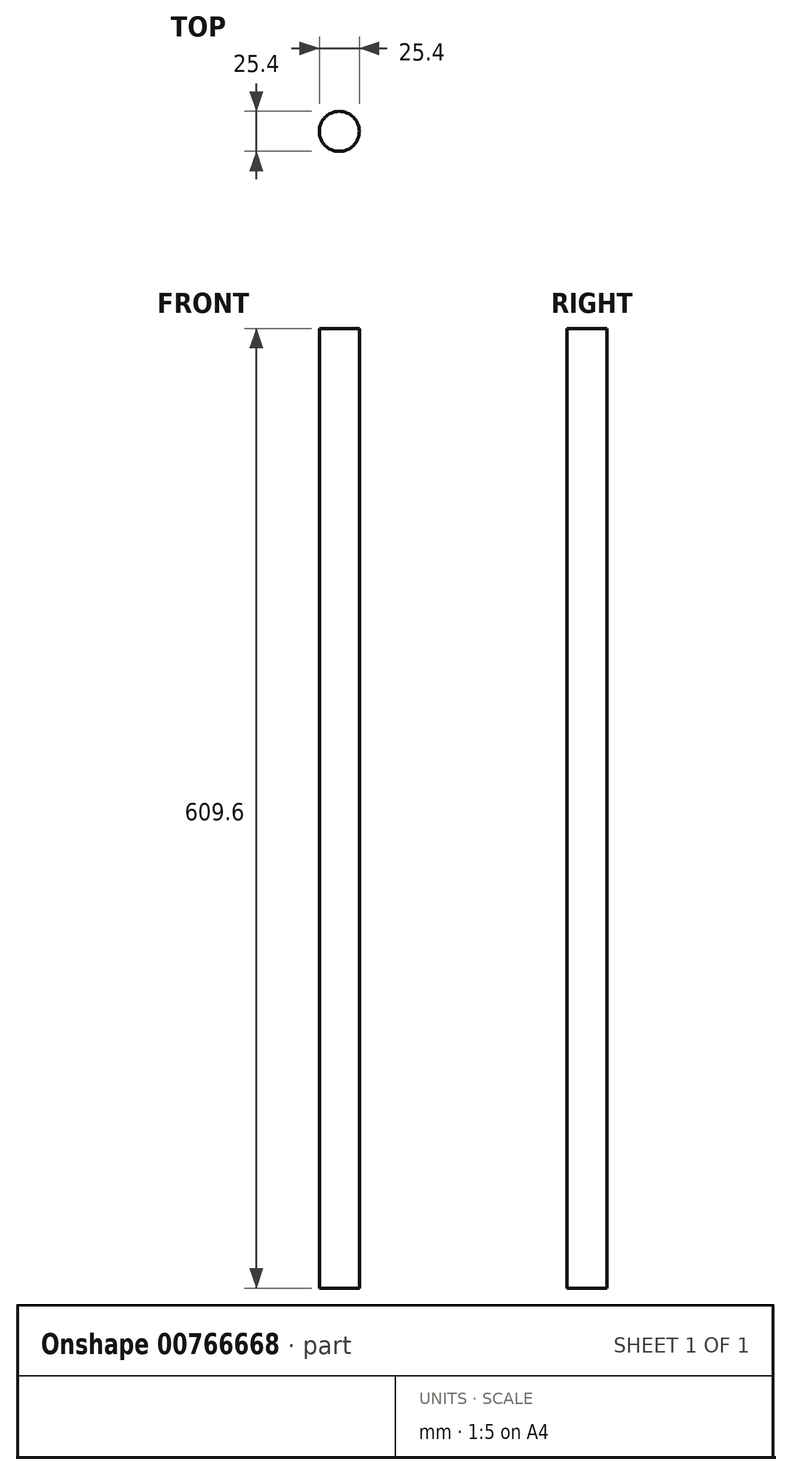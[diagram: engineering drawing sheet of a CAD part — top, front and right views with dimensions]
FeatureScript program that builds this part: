
annotation { "Feature Type Name" : "Feature", "Feature Type Description" : "" }
export const myFeature = defineFeature(function(context is Context, id is Id, definition is map)
    precondition{}
    {
        {
            var Q0;
            Q0=qCreatedBy(makeId("Top.planeOp"),FACE);
            var sketch = newSketch(context, id + "F0", { "sketchPlane" : qUnion([Q0])});
            skCircle(sketch, "E0", {"center": v(0, 0) * mm, "radius": 12.7 * mm});
            skSolve(sketch);
        }
        {
            var Q0;
            Q0 = qSketchRegion(id + "F0", true);
            extrude(context, id + "F1", {"entities" : qUnion([Q0]), "endBound" : BoundingType.SYMMETRIC, "depth" : 609.6 * mm, "offsetDistance" : 25.4 * mm});
        }
    });
